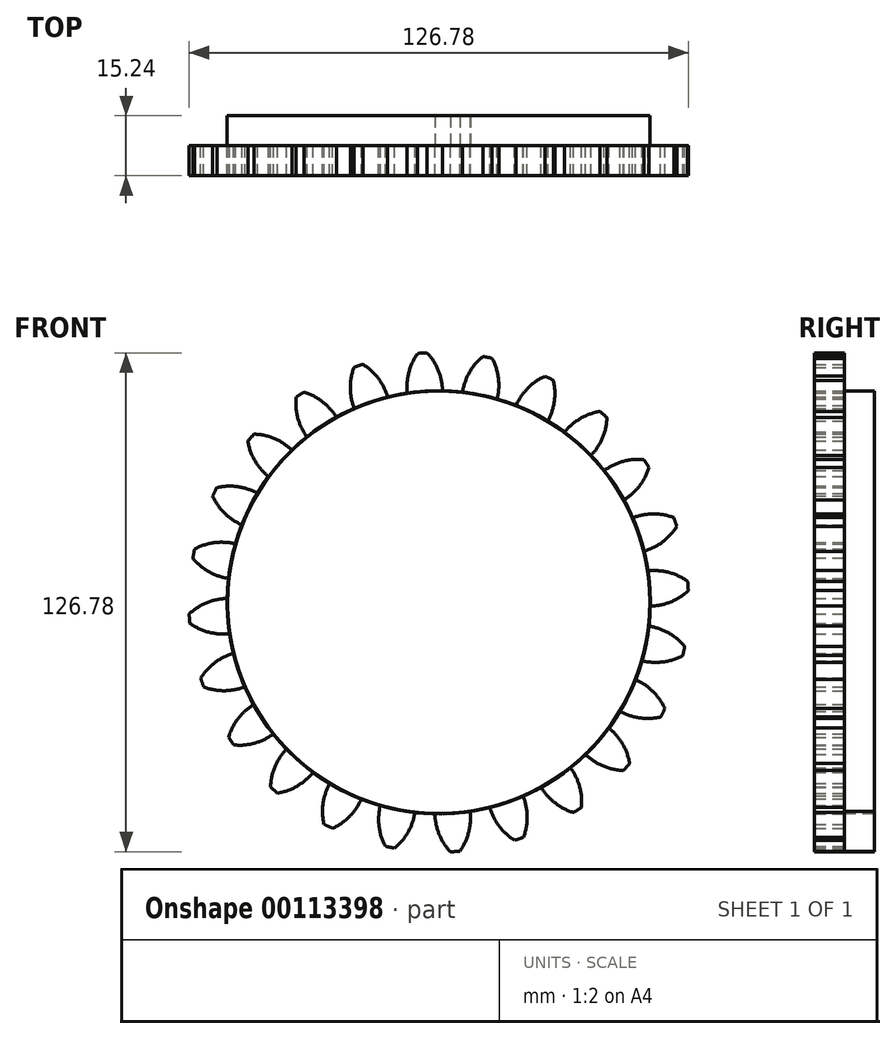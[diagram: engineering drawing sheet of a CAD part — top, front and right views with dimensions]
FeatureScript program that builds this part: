
annotation { "Feature Type Name" : "Feature", "Feature Type Description" : "" }
export const myFeature = defineFeature(function(context is Context, id is Id, definition is map)
    precondition{}
    {
        {
            var Q0;
            Q0=qCreatedBy(makeId("Front.planeOp"),FACE);
            var sketch = newSketch(context, id + "F0", { "sketchPlane" : qUnion([Q0])});
            skCircle(sketch, "E0", {"center": v(0, 0) * mm, "radius": 53.72 * mm});
            skCircle(sketch, "E1", {"center": v(0, 0) * mm, "radius": 58.67 * mm, "construction": true});
            skCircle(sketch, "E2", {"center": v(0, 0) * mm, "radius": 63.5 * mm, "construction": true});
            skLineSegment(sketch, "E3", {"start": v(0, 0) * mm, "end": v(0, 90.64) * mm, "construction": true});
            skLineSegment(sketch, "E4", {"start": v(0, 0) * mm, "end": v(-5.92, 90.33) * mm, "construction": true});
            skLineSegment(sketch, "E5", {"start": v(0, 58.67) * mm, "end": v(-89.6, 58.67) * mm, "construction": true});
            skLineSegment(sketch, "E6", {"start": v(0, 58.67) * mm, "end": v(-90.31, 25.8) * mm, "construction": true});
            skCircle(sketch, "E7", {"center": v(0, 58.67) * mm, "radius": 14.6 * mm, "construction": true});
            skCircle(sketch, "E8", {"center": v(0, 0) * mm, "radius": 55.14 * mm, "construction": true});
            skCircle(sketch, "E9", {"center": v(-13.62, 53.4) * mm, "radius": 14.6 * mm, "construction": true});
            skArc(sketch, "E10", {"start": v(0, 58.67) * mm, "mid": v(-1.25, 61.18) * mm, "end": v(-2.96, 63.4) * mm});
            skArc(sketch, "E11", {"start": v(0.98, 53.71) * mm, "mid": v(0.7, 56.23) * mm, "end": v(0, 58.67) * mm});
            skArc(sketch, "E12.MirrorCS", {"start": v(-7.66, 58.17) * mm, "mid": v(-6.75, 60.82) * mm, "end": v(-5.34, 63.24) * mm});
            skArc(sketch, "E13.MirrorCS", {"start": v(-7.98, 53.12) * mm, "mid": v(-8.03, 55.66) * mm, "end": v(-7.66, 58.17) * mm});
            skArc(sketch, "E14", {"start": v(-2.96, 63.4) * mm, "mid": v(-4.15, 63.34) * mm, "end": v(-5.34, 63.24) * mm});
            skSolve(sketch);
        }
        {
            var Q0;
            {var subQ0=sQuery(id+"F0.wireOp",EDGE,"E0");var subQ1=makeQuery(id+"F0.imprint","INTERSECT",VERTEX,{"derivedFrom":[subQ0,sQuery(id+"F0.wireOp",EDGE,"E11")]});Q0=makeQuery(id+"F0.imprint","IMPRINT",FACE,{"disambiguationData":[TD([[makeQuery(id+"F0.imprint","IMPRINT",EDGE,{"disambiguationData":[TD([[subQ1,-1.0]])],"derivedFrom":subQ0}),1.0]])]});}
            var Q1;
            Q1=makeQuery(id+"F0.imprint","IMPRINT",FACE,{"disambiguationData":[TD([[makeQuery(id+"F0.imprint","IMPRINT",EDGE,{"derivedFrom":sQuery(id+"F0.wireOp",EDGE,"E10")}),1.0]])]});
            extrude(context, id + "F1", {"entities" : qUnion([Q0, Q1]), "depth" : 7.62 * mm});
        }
        {
            var Q0;
            Q0=makeQuery(id+"F1.opExtrude","SWEPT_BODY",BODY,{"disambiguationData":[OSD([sQuery(id+"F0.wireOp",EDGE,"E0"),sQuery(id+"F0.wireOp",EDGE,"E10"),sQuery(id+"F0.wireOp",EDGE,"E11"),sQuery(id+"F0.wireOp",EDGE,"E12.MirrorCS"),sQuery(id+"F0.wireOp",EDGE,"E13.MirrorCS"),sQuery(id+"F0.wireOp",EDGE,"E14")])]});
            var Q1;
            Q1=makeQuery(id+"F1.opExtrude","SWEPT_FACE",FACE,{"disambiguationData":[OSD([sQuery(id+"F0.wireOp",EDGE,"E0")])]});
            circularPattern(context, id + "F2", {"entities" : qUnion([Q0]), "axis" : qUnion([Q1]), "angle" : 15 * degree, "instanceCount" : 24});
        }
        {
            var Q0;
            Q0=makeQuery(id+"F2.opPattern","COPY",BODY,{"derivedFrom":makeQuery(id+"F1.opExtrude","SWEPT_BODY",BODY,{"disambiguationData":[OSD([sQuery(id+"F0.wireOp",EDGE,"E0"),sQuery(id+"F0.wireOp",EDGE,"E10"),sQuery(id+"F0.wireOp",EDGE,"E11"),sQuery(id+"F0.wireOp",EDGE,"E12.MirrorCS"),sQuery(id+"F0.wireOp",EDGE,"E13.MirrorCS"),sQuery(id+"F0.wireOp",EDGE,"E14")])]}),"instanceName":"12"});
            var Q1;
            Q1=qCreatedBy(makeId("Front.planeOp"),FACE);
            mirror(context, id + "F3", {"entities" : qUnion([Q0]), "mirrorPlane" : qUnion([Q1])});
        }
    });
